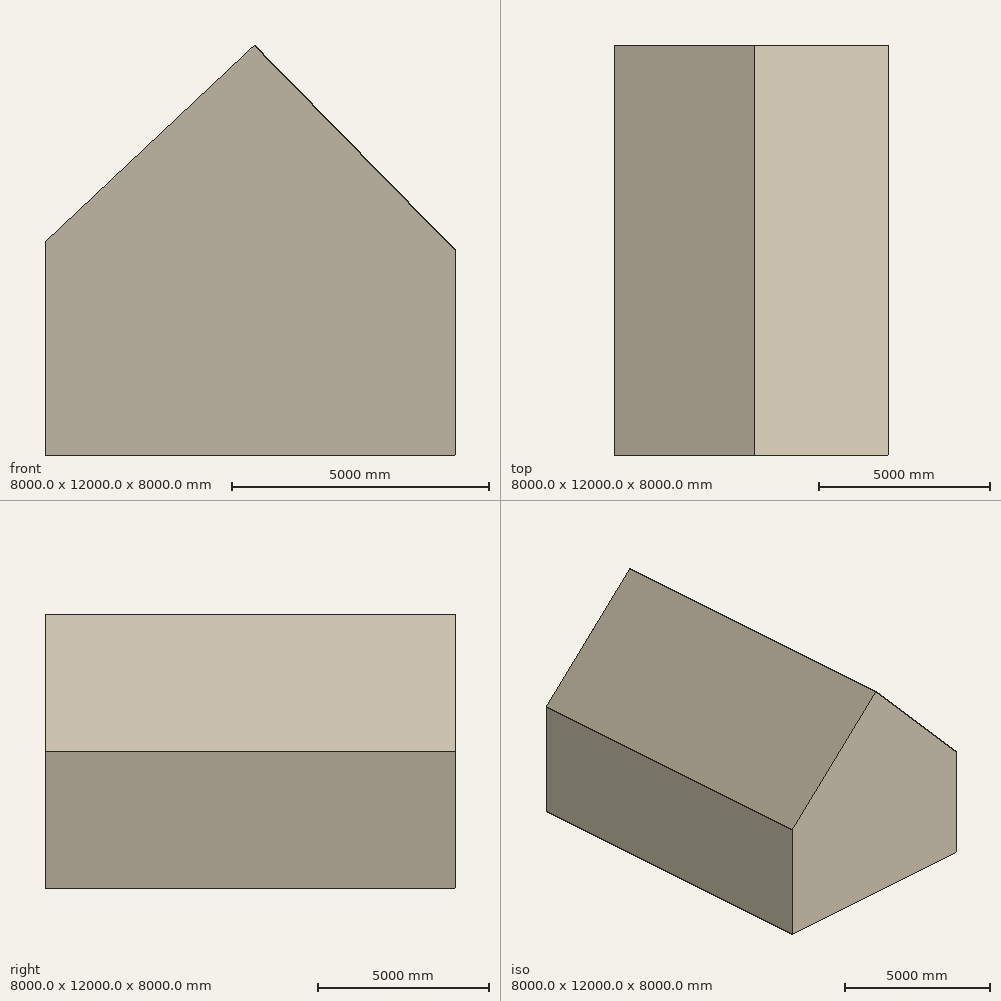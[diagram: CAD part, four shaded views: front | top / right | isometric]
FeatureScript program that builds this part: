
annotation { "Feature Type Name" : "Feature", "Feature Type Description" : "" }
export const myFeature = defineFeature(function(context is Context, id is Id, definition is map)
    precondition{}
    {
        {
            var Q0;
            Q0=qCreatedBy(makeId("Front.planeOp"),FACE);
            var sketch = newSketch(context, id + "F0", { "sketchPlane" : qUnion([Q0])});
            skLineSegment(sketch, "E0", {"start": v(0, 0) * mm, "end": v(-8000, 0) * mm});
            skLineSegment(sketch, "E1", {"start": v(-8000, 0) * mm, "end": v(-8000, 4165.04) * mm});
            skLineSegment(sketch, "E2", {"start": v(0, 0) * mm, "end": v(0, 4000) * mm});
            skLineSegment(sketch, "E3", {"start": v(0, 4000) * mm, "end": v(-3919.18, 8000) * mm});
            skLineSegment(sketch, "E4", {"start": v(-3919.18, 8000) * mm, "end": v(-8000, 4165.04) * mm});
            skSolve(sketch);
        }
        {
            var Q0;
            Q0=makeQuery(id+"F0.imprint","IMPRINT",FACE,{"disambiguationData":[TD([[makeQuery(id+"F0.imprint","IMPRINT",EDGE,{"derivedFrom":sQuery(id+"F0.wireOp",EDGE,"E0")}),-1.0]])]});
            extrude(context, id + "F1", {"entities" : qUnion([Q0]), "depth" : 12000 * mm});
        }
    });
